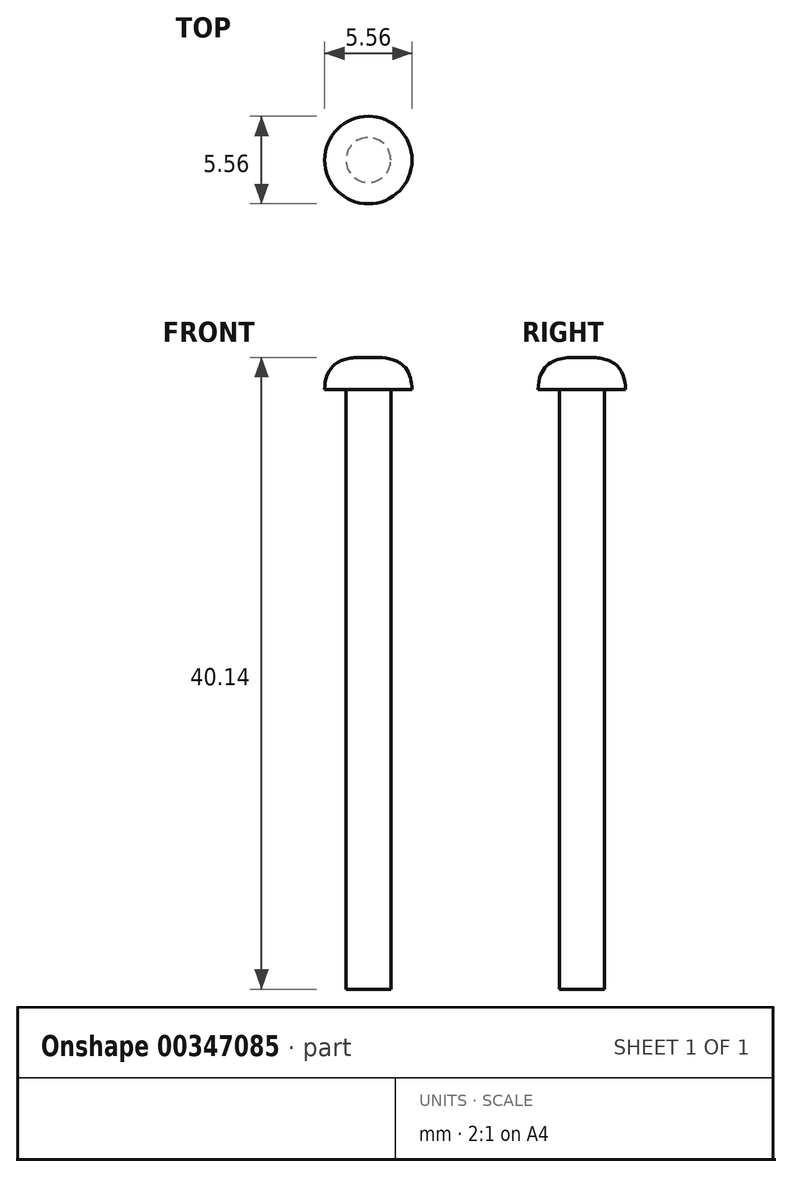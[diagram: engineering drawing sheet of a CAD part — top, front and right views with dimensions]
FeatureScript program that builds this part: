
annotation { "Feature Type Name" : "Feature", "Feature Type Description" : "" }
export const myFeature = defineFeature(function(context is Context, id is Id, definition is map)
    precondition{}
    {
        {
            var Q0;
            Q0=qCreatedBy(makeId("Top.planeOp"),FACE);
            var sketch = newSketch(context, id + "F0", { "sketchPlane" : qUnion([Q0])});
            skCircle(sketch, "E0", {"center": v(0, 0) * mm, "radius": 1.42 * mm});
            skSolve(sketch);
        }
        {
            var Q0;
            Q0 = qSketchRegion(id + "F0", true);
            extrude(context, id + "F1", {"entities" : qUnion([Q0]), "oppositeDirection" : true, "depth" : 38.1 * mm, "offsetDistance" : 25 * mm});
        }
        {
            var Q0;
            Q0=qCreatedBy(makeId("Right.planeOp"),FACE);
            var sketch = newSketch(context, id + "F2", { "sketchPlane" : qUnion([Q0])});
            skFitSpline(sketch, "E1", {"points": [v(-2.78, 0) * mm, v(0, 2.03) * mm], "startDerivative": vector(0.18, 6.27) * mm, "endDerivative": vector(3.19, -0.1) * mm});
            skLineSegment(sketch, "E2", {"start": v(-2.78, 0) * mm, "end": v(0, 0) * mm});
            skLineSegment(sketch, "E3", {"start": v(0, 0) * mm, "end": v(0, 2.03) * mm});
            skSolve(sketch);
        }
        {
            var Q0;
            Q0 = qSketchRegion(id + "F2", true);
            var Q1;
            Q1=sQuery(id+"F2.wireOp",EDGE,"E3");
            revolve(context, id + "F3", {"operationType" : NewBodyOperationType.ADD, "entities" : qUnion([Q0]), "axis" : qUnion([Q1]), "revolveType" : RevolveType.FULL});
        }
    });
